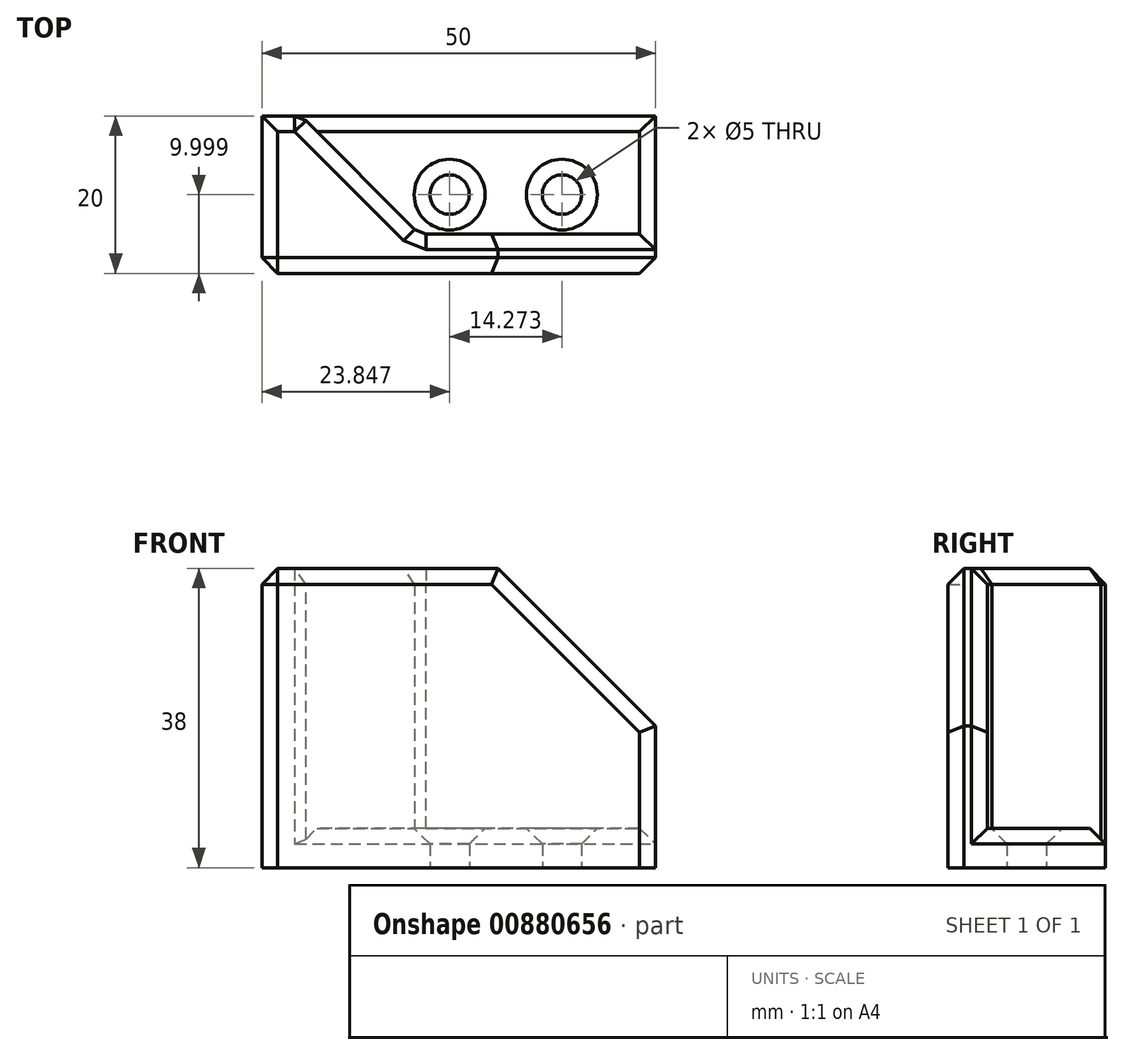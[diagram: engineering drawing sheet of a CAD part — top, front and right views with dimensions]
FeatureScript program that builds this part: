
annotation { "Feature Type Name" : "Feature", "Feature Type Description" : "" }
export const myFeature = defineFeature(function(context is Context, id is Id, definition is map)
    precondition{}
    {
        {
            var Q0;
            Q0=qCreatedBy(makeId("Top.planeOp"),FACE);
            var sketch = newSketch(context, id + "F0", { "sketchPlane" : qUnion([Q0])});
            skLineSegment(sketch, "E0.right", {"start": v(-45.34, 30.7) * mm, "end": v(-45.34, 10.7) * mm});
            skLineSegment(sketch, "E1.right", {"start": v(-95.34, 30.7) * mm, "end": v(-95.34, 10.7) * mm});
            skPoint(sketch, "E2.positionSnap0", {"position": v(-15.34, 20.7) * mm});
            skPoint(sketch, "E3.positionSnap0", {"position": v(-45.34, 20.7) * mm});
            skCircle(sketch, "E4", {"center": v(-57.22, 20.7) * mm, "radius": 2.5 * mm});
            skCircle(sketch, "E5", {"center": v(-71.5, 20.7) * mm, "radius": 2.5 * mm});
            skLineSegment(sketch, "E6", {"start": v(-95.34, 10.7) * mm, "end": v(-45.34, 10.7) * mm});
            skLineSegment(sketch, "E7", {"start": v(-95.34, 30.7) * mm, "end": v(-45.34, 30.7) * mm});
            skLineSegment(sketch, "E8.0", {"start": v(-75.34, 15.7) * mm, "end": v(-45.34, 15.7) * mm});
            skPoint(sketch, "E9", {"position": v(-75.34, 15.7) * mm});
            skLineSegment(sketch, "E10", {"start": v(-90.34, 30.7) * mm, "end": v(-75.34, 15.7) * mm});
            skSolve(sketch);
        }
        {
            var Q0;
            Q0=makeQuery(id+"F0.imprint","IMPRINT",FACE,{"disambiguationData":[TD([[makeQuery(id+"F0.imprint","IMPRINT",EDGE,{"derivedFrom":sQuery(id+"F0.wireOp",EDGE,"E4")}),-1.0]])]});
            extrude(context, id + "F1", {"entities" : qUnion([Q0]), "depth" : 5 * mm, "offsetDistance" : 25 * mm});
        }
        {
            var Q0;
            {var subQ1=sQuery(id+"F0.wireOp",EDGE,"E1.right");Q0=makeQuery(id+"F0.imprint","IMPRINT",FACE,{"disambiguationData":[TD([[makeQuery(id+"F0.imprint","IMPRINT",EDGE,{"derivedFrom":subQ1}),1.0]])]});}
            extrude(context, id + "F2", {"entities" : qUnion([Q0]), "operationType" : NewBodyOperationType.ADD, "depth" : 38 * mm, "offsetDistance" : 25 * mm});
        }
        {
            var Q0;
            Q0=makeQuery(id+"F2.opExtrude","CAP_EDGE",EDGE,{"disambiguationData":[OSD([sQuery(id+"F0.wireOp",EDGE,"E0.right")])],"isStart":false});
            chamfer(context, id + "F3", {"entities" : qUnion([Q0]), "width" : 20 * mm, "tangentPropagation" : true});
        }
        {
            var Q0;
            Q0=makeQuery(id+"F1.opExtrude","CAP_EDGE",EDGE,{"disambiguationData":[OSD([sQuery(id+"F0.wireOp",EDGE,"E5")])],"isStart":false});
            var Q1;
            Q1=makeQuery(id+"F1.opExtrude","CAP_EDGE",EDGE,{"disambiguationData":[OSD([sQuery(id+"F0.wireOp",EDGE,"E4")])],"isStart":false});
            chamfer(context, id + "F4", {"entities" : qUnion([Q0, Q1]), "width" : 2 * mm, "tangentPropagation" : true});
        }
        {
            var Q0;
            Q0=makeQuery(id+"F2.opExtrude","CAP_EDGE",EDGE,{"disambiguationData":[OSD([sQuery(id+"F0.wireOp",EDGE,"E1.right")])],"isStart":false});
            var Q1;
            Q1=makeQuery(id+"F2.opExtrude","CAP_EDGE",EDGE,{"disambiguationData":[OSD([sQuery(id+"F0.wireOp",EDGE,"E6")])],"isStart":false});
            var Q2;
            Q2=makeQuery(id+"F2.opExtrude","CAP_EDGE",EDGE,{"disambiguationData":[OSD([sQuery(id+"F0.wireOp",EDGE,"E10")])],"isStart":false});
            var Q3;
            Q3=makeQuery(id+"F2.opExtrude","CAP_EDGE",EDGE,{"disambiguationData":[OSD([sQuery(id+"F0.wireOp",EDGE,"E8.0")])],"isStart":false});
            var Q4;
            Q4=makeQuery(id+"F2.opExtrude","CAP_EDGE",EDGE,{"disambiguationData":[OSD([sQuery(id+"F0.wireOp",EDGE,"E7")])],"isStart":false});
            var Q5;
            Q5=makeQuery(id+"F2.opExtrude","SWEPT_EDGE",EDGE,{"disambiguationData":[OSD([sQuery(id+"F0.wireOp",EDGE,"E1.right"),sQuery(id+"F0.wireOp",EDGE,"E6")])]});
            var Q6;
            Q6=makeQuery(id+"F3.opChamfer","BLEND_EDGE",EDGE,{"blendedFrom":[makeQuery(id+"F2.opExtrude","CAP_EDGE",EDGE,{"disambiguationData":[OSD([sQuery(id+"F0.wireOp",EDGE,"E0.right")])],"isStart":false}),makeQuery(id+"F2.opExtrude","SWEPT_FACE",FACE,{"disambiguationData":[OSD([sQuery(id+"F0.wireOp",EDGE,"E6")])]})],"blendedInto":[makeQuery(id+"F2.opExtrude","SWEPT_FACE",FACE,{"disambiguationData":[OSD([sQuery(id+"F0.wireOp",EDGE,"E6")])]})]});
            var Q7;
            Q7=makeQuery(id+"F2.opExtrude","SWEPT_EDGE",EDGE,{"disambiguationData":[OSD([sQuery(id+"F0.wireOp",EDGE,"E0.right"),sQuery(id+"F0.wireOp",EDGE,"E6")])]});
            var Q8;
            Q8=makeQuery(id+"F3.opChamfer","BLEND_EDGE",EDGE,{"blendedFrom":[makeQuery(id+"F2.opExtrude","CAP_EDGE",EDGE,{"disambiguationData":[OSD([sQuery(id+"F0.wireOp",EDGE,"E0.right")])],"isStart":false}),makeQuery(id+"F2.opExtrude","SWEPT_FACE",FACE,{"disambiguationData":[OSD([sQuery(id+"F0.wireOp",EDGE,"E8.0")])]})],"blendedInto":[makeQuery(id+"F2.opExtrude","SWEPT_FACE",FACE,{"disambiguationData":[OSD([sQuery(id+"F0.wireOp",EDGE,"E8.0")])]})]});
            var Q9;
            Q9=makeQuery(id+"F2.opExtrude","SWEPT_EDGE",EDGE,{"disambiguationData":[OSD([sQuery(id+"F0.wireOp",EDGE,"E0.right"),sQuery(id+"F0.wireOp",EDGE,"E8.0")])]});
            var Q10;
            Q10=makeQuery(id+"F1.opExtrude","CAP_EDGE",EDGE,{"disambiguationData":[OSD([sQuery(id+"F0.wireOp",EDGE,"E0.right")])],"isStart":false});
            var Q11;
            Q11=makeQuery(id+"F2.opExtrude","SWEPT_EDGE",EDGE,{"disambiguationData":[OSD([sQuery(id+"F0.wireOp",EDGE,"E8.0"),sQuery(id+"F0.wireOp",EDGE,"E10")])]});
            var Q12;
            Q12=makeQuery(id+"F2.opExtrude","SWEPT_EDGE",EDGE,{"disambiguationData":[OSD([sQuery(id+"F0.wireOp",EDGE,"E7"),sQuery(id+"F0.wireOp",EDGE,"E10")])]});
            var Q13;
            Q13=makeQuery(id+"F1.opExtrude","CAP_EDGE",EDGE,{"disambiguationData":[OSD([sQuery(id+"F0.wireOp",EDGE,"E7")])],"isStart":false});
            chamfer(context, id + "F5", {"entities" : qUnion([Q0, Q1, Q2, Q3, Q4, Q5, Q6, Q7, Q8, Q9, Q10, Q11, Q12, Q13]), "width" : 2 * mm, "tangentPropagation" : true});
        }
    });
